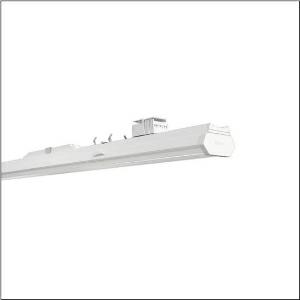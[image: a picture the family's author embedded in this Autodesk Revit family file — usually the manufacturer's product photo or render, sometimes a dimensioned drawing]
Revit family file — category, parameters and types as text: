
# Revit family: licross_21_protected_mo_52tp11mn4a5g
name_source: partatom
category: Lighting Fixtures
units: mm (PartAtom-declared; Revit-internal decimal feet)

## family parameters
Cut with Voids When Loaded = No
Host = Face
Light Source = No
Part Type = Normal
Room Calculation Point = No
Round Connector Dimension = Use Diameter
Shared = No

## types (1)
- --- (1 x LED, 10700 lm, 60.5 W, 4000K)
    Apparent Load = 61 VA
    CIE Flux Codes = 83 94 98 100 100
    Color Rendering = 80
    Color Temperature = 4000K
    Default Elevation = 1800 mm
    Description = Licross 21 Protected MO, luminaire insert, of sheet steel, galvanised, coil coated, white, length: 1.500mm, width: 66mm, height: 67mm, LED rated luminous flux: 10.700lm, light colour: 840, SDCM (Standard Deviation of Colour Matching)MacAdam ≤ 3 SDCM (initial), control gear: ON/OFF Multilumen, with plug, 3-pole, with phase selection, mains connection: 220..240V, AC, 50/60Hz, rated input power: 61W, internal wiring halogen-free, primary light control with lens, of plastic, primary optical cover: cover, of PMMA, light emission: direct distribution, primary light characteristic: symmetric, protection rating (complete): IP64, insulation class (complete): insulation class I (protective earthing), certification: CE, ENEC, VDE, UKCA, protection symbol: D if used in an environment with conductive dust loads with corresponding accessories, impact resistance: IK06, permissible ambient temperature for indoor applications: -35..+45°C, corresponds to IFS (International Featured Standards) requirements for safety and quality in the food industry, reducing of maximum allowable ambient temperature of 5°C with ceiling mounting, LABS conformity tested according to VDMA 24364:2018-05, The light source and the operating device comply with the requirements of the Ecodesign Regulation (EU) 2019/2020 and are replaceable in accordance with this regulation, packaging unit: 1 piece
    Height = 92 mm
    Lamp = 1 x LED
    Lamp Light Flux = 10700 lm
    Lamp Power = 60.5 W
    Lamp count = 1
    Length = 1500 mm
    Luminous efficacy = 177 lm/W
    Manufacturer = Siteco
    ModVariant = No
    Model = 52TP11MN4A5G
    Mounting Place = Ceiling
    Mounting Type = Pendant
    Number of Poles = 1
    OnlyDefault = Yes
    Power Factor = 1
    Product Name = Licross 21 Protected MO
    Product group = luminaire insert | ceiling pendant
    ProductGroupID = 901
    Protection Class = Protection class I
    Protection Degree = IP 64
    RLX_Detail_Level = 1
    RLX_Emergency_Light_Flux = 0 lm
    RLX_Emergency_Type = 0
    RLX_Emergency_Type_DB = No
    RlxData = <blob elided: 22069 chars, md5=5653b539>
    Socket = socket
    Standby Power = 0 W
    System Light Flux = 10700 lm
    System Power = 61 W
    Type Comments = factory setting: luminous flux: 100 % | (A | C | E) | 140 mA
    Type Image = l_1256148.jpg
    URL = http://relux.com
    VarID = @adj_109007
    Voltage = 0 V
    Weight = 0.00 kg
    Width = 88 mm

## geometry (parser evidence)
native form markers: Blend x4, Sweep x9
no freeform markers — native parametric forms only
